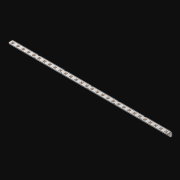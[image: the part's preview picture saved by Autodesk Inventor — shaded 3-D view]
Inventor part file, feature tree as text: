
AUTODESK INVENTOR PART (.ipt)
format: ipt  version: 2021 (Build 250183000, 183)  size: 822,272 bytes
history: native  units: in
note: dims shown in document units (in); Inventor stores cm internally (conversion verified against a paired STEP export)
features: extrude x61, other x60, sketch x3, pattern_linear x1, sheet_metal_op x1
ambient origin geometry x8: Origin, YZ Plane, XZ Plane, XY Plane, X Axis, Y Axis, Z Axis, Center Point
bodies: Solid1 (feature_tree)
feature tree (126):
  pattern_linear  "Rectangular Pattern1"  Spacing1=0.063in  [1 undecoded]
  extrude  "Extrusion1"  Depth=0.5in
  sketch  "Sketch1"  dims[d0=0.182in]
  other  "Srf1"
  sketch  "Sketch2"  dims[d1=0.063in d2=0.0in]
  other  "Srf2"
  other  "Srf3"
  other  "Srf5"
  other  "Srf7"
  other  "Srf9"
  other  "Srf11"
  other  "Srf13"
  other  "Srf15"
  other  "Srf17"
  other  "Srf19"
  other  "Srf21"
  other  "Srf23"
  other  "Srf25"
  other  "Srf27"
  other  "Srf29"
  other  "Srf31"
  other  "Srf33"
  other  "Srf35"
  other  "Srf37"
  other  "Srf39"
  other  "Srf41"
  other  "Srf43"
  other  "Srf45"
  other  "Srf47"
  other  "Srf49"
  other  "Srf51"
  other  "Srf53"
  other  "Srf55"
  other  "Srf57"
  other  "Srf59"
  other  "Srf4"
  other  "Srf6"
  other  "Srf8"
  other  "Srf10"
  other  "Srf12"
  other  "Srf14"
  other  "Srf16"
  other  "Srf18"
  other  "Srf20"
  other  "Srf22"
  other  "Srf24"
  other  "Srf26"
  other  "Srf28"
  other  "Srf30"
  other  "Srf32"
  other  "Srf34"
  other  "Srf36"
  other  "Srf38"
  other  "Srf40"
  other  "Srf42"
  other  "Srf44"
  other  "Srf46"
  other  "Srf48"
  other  "Srf50"
  other  "Srf52"
  other  "Srf54"
  other  "Srf56"
  other  "Srf58"
  other  "Srf60"
  sketch  "Sketch3"  dims[d3=0.182in d4=0.063in d5=0.0in d8=0.5in d9=2.5in d10=0.0in]
  sheet_metal_op  "Fold1"
  extrude  "ExtrusionSrf1"  Depth=0.5in TaperAngle=0.0deg
  extrude  "ExtrusionSrf2"  [1 undecoded]
  extrude  "ExtrusionSrf3"  [1 undecoded]
  extrude  "ExtrusionSrf4"  [1 undecoded]
  extrude  "ExtrusionSrf5"  [1 undecoded]
  extrude  "ExtrusionSrf6"  [1 undecoded]
  extrude  "ExtrusionSrf7"  [1 undecoded]
  extrude  "ExtrusionSrf8"  [1 undecoded]
  extrude  "ExtrusionSrf9"  [1 undecoded]
  extrude  "ExtrusionSrf10"  [1 undecoded]
  extrude  "ExtrusionSrf11"  [1 undecoded]
  extrude  "ExtrusionSrf12"  [1 undecoded]
  extrude  "ExtrusionSrf13"  [1 undecoded]
  extrude  "ExtrusionSrf14"  [1 undecoded]
  extrude  "ExtrusionSrf15"  [1 undecoded]
  extrude  "ExtrusionSrf16"  [1 undecoded]
  extrude  "ExtrusionSrf17"  [1 undecoded]
  extrude  "ExtrusionSrf18"  [1 undecoded]
  extrude  "ExtrusionSrf19"  [1 undecoded]
  extrude  "ExtrusionSrf20"  [1 undecoded]
  extrude  "ExtrusionSrf21"  [1 undecoded]
  extrude  "ExtrusionSrf22"  [1 undecoded]
  extrude  "ExtrusionSrf23"  [1 undecoded]
  extrude  "ExtrusionSrf24"  [1 undecoded]
  extrude  "ExtrusionSrf25"  [1 undecoded]
  extrude  "ExtrusionSrf26"  [1 undecoded]
  extrude  "ExtrusionSrf27"  [1 undecoded]
  extrude  "ExtrusionSrf28"  [1 undecoded]
  extrude  "ExtrusionSrf29"  [1 undecoded]
  extrude  "ExtrusionSrf30"  [1 undecoded]
  extrude  "ExtrusionSrf31"  [1 undecoded]
  extrude  "ExtrusionSrf37"  [1 undecoded]
  extrude  "ExtrusionSrf38"  [1 undecoded]
  extrude  "ExtrusionSrf39"  [1 undecoded]
  extrude  "ExtrusionSrf40"  [1 undecoded]
  extrude  "ExtrusionSrf41"  [1 undecoded]
  extrude  "ExtrusionSrf42"  [1 undecoded]
  extrude  "ExtrusionSrf43"  [1 undecoded]
  extrude  "ExtrusionSrf44"  [1 undecoded]
  extrude  "ExtrusionSrf45"  [1 undecoded]
  extrude  "ExtrusionSrf46"  [1 undecoded]
  extrude  "ExtrusionSrf47"  [1 undecoded]
  extrude  "ExtrusionSrf48"  [1 undecoded]
  extrude  "ExtrusionSrf49"  [1 undecoded]
  extrude  "ExtrusionSrf50"  [1 undecoded]
  extrude  "ExtrusionSrf51"  [1 undecoded]
  extrude  "ExtrusionSrf52"  [1 undecoded]
  extrude  "ExtrusionSrf53"  [1 undecoded]
  extrude  "ExtrusionSrf54"  [1 undecoded]
  extrude  "ExtrusionSrf55"  [1 undecoded]
  extrude  "ExtrusionSrf56"  [1 undecoded]
  extrude  "ExtrusionSrf57"  [1 undecoded]
  extrude  "ExtrusionSrf58"  [1 undecoded]
  extrude  "ExtrusionSrf59"  [1 undecoded]
  extrude  "ExtrusionSrf60"  [1 undecoded]
  extrude  "ExtrusionSrf61"  [1 undecoded]
  extrude  "ExtrusionSrf62"  [1 undecoded]
  extrude  "ExtrusionSrf63"  [1 undecoded]
  extrude  "ExtrusionSrf64"  [1 undecoded]
  extrude  "ExtrusionSrf65"  [1 undecoded]
note: 60 required parameter values undecoded (feature->parameter linkage not recoverable at this tier; creation-order binding heuristic only, values carry confidence <= 0.55)
